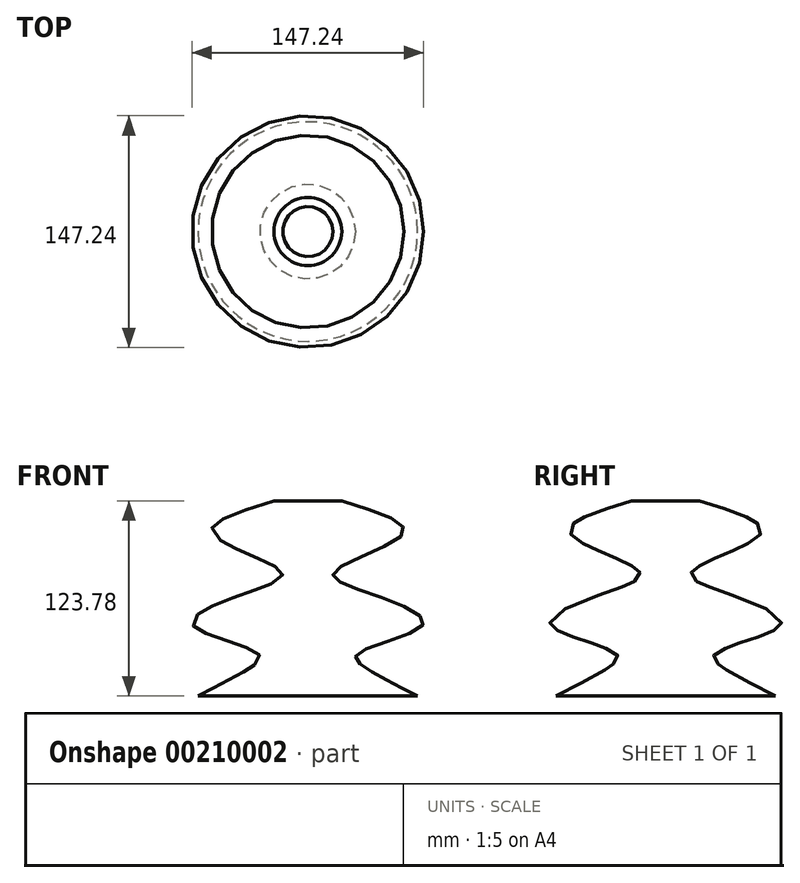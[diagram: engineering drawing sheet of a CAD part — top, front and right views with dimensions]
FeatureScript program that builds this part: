
annotation { "Feature Type Name" : "Feature", "Feature Type Description" : "" }
export const myFeature = defineFeature(function(context is Context, id is Id, definition is map)
    precondition{}
    {
        {
            var Q0;
            Q0=qCreatedBy(makeId("Front.planeOp"),FACE);
            var sketch = newSketch(context, id + "F0", { "sketchPlane" : qUnion([Q0])});
            skFitSpline(sketch, "E0", {"points": [v(21.57, 53.6) * mm, v(60.64, 32.98) * mm, v(16.57, 8.6) * mm, v(38.76, -4.85) * mm, v(73.14, -25.16) * mm, v(30.95, -43.92) * mm, v(38.13, -53.3) * mm, v(69.7, -70.17) * mm], "startDerivative": vector(405.82, -121.6) * mm, "endDerivative": vector(232.97, -117.59) * mm});
            skLineSegment(sketch, "E1", {"start": v(0, 57.83) * mm, "end": v(0, 71.27) * mm});
            skSolve(sketch);
        }
        {
            var Q0;
            Q0=sQuery(id+"F0.wireOp",EDGE,"E0");
            var Q1;
            Q1=sQuery(id+"F0.wireOp",EDGE,"E1");
            revolve(context, id + "F1", {"bodyType" : ToolBodyType.SURFACE, "surfaceEntities" : qUnion([Q0]), "axis" : qUnion([Q1]), "revolveType" : RevolveType.FULL});
        }
    });
